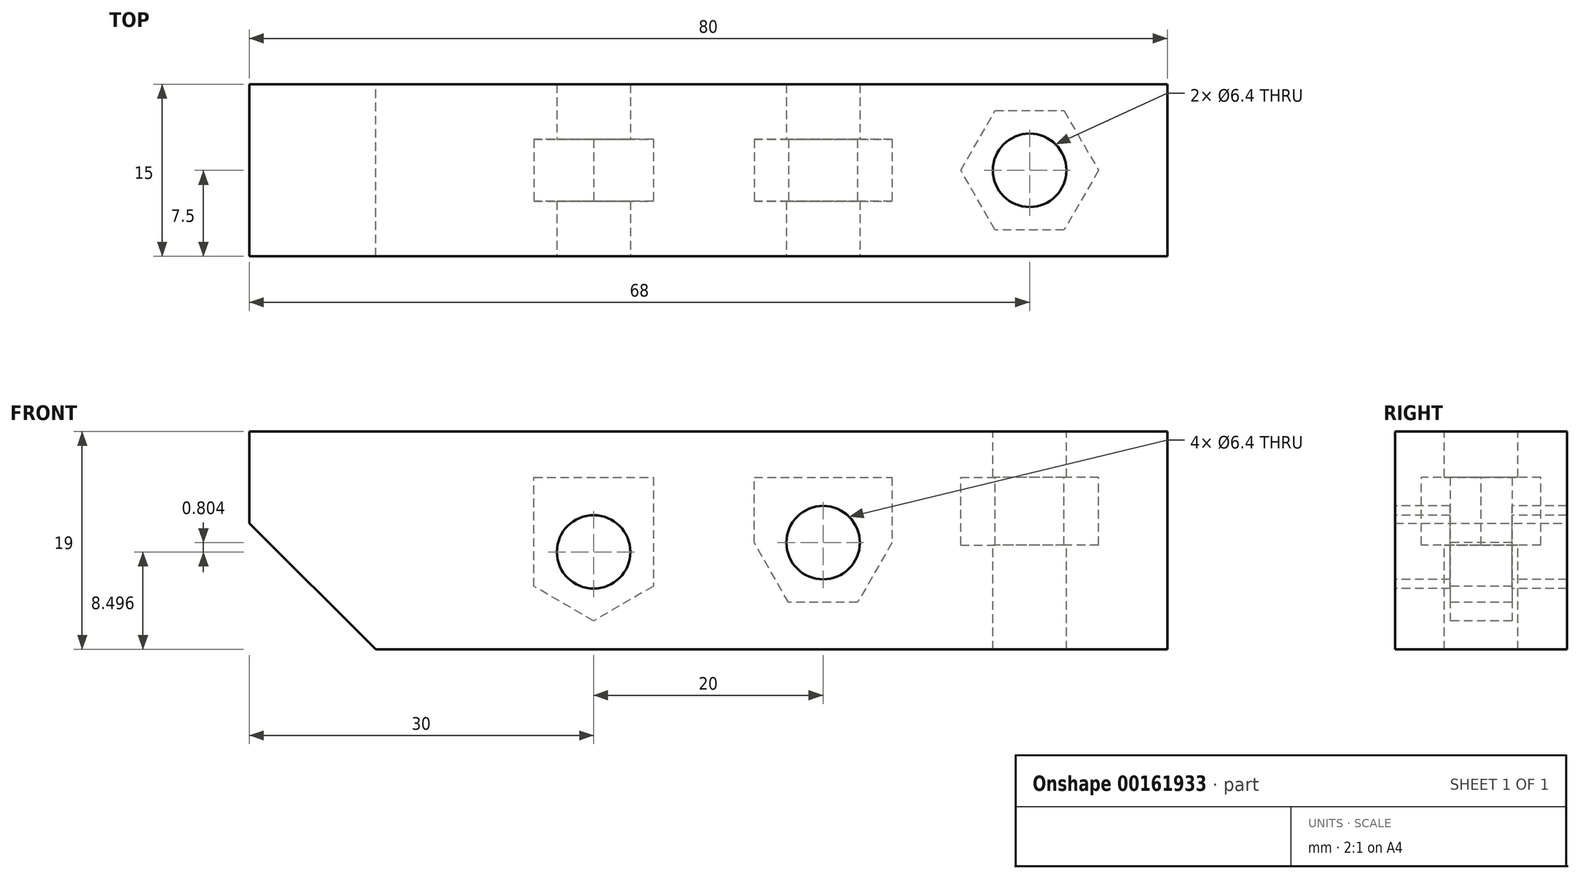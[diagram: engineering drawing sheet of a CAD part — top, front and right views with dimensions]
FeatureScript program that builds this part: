
annotation { "Feature Type Name" : "Feature", "Feature Type Description" : "" }
export const myFeature = defineFeature(function(context is Context, id is Id, definition is map)
    precondition{}
    {
        {
            var Q0;
            Q0=qCreatedBy(makeId("Front.planeOp"),FACE);
            var sketch = newSketch(context, id + "F0", { "sketchPlane" : qUnion([Q0])});
            skLineSegment(sketch, "E0", {"start": v(0, 0) * mm, "end": v(-69, 0) * mm});
            skLineSegment(sketch, "E1", {"start": v(-69, 0) * mm, "end": v(-80, 11) * mm});
            skLineSegment(sketch, "E2", {"start": v(-80, 11) * mm, "end": v(-80, 15) * mm});
            skLineSegment(sketch, "E3", {"start": v(-80, 15) * mm, "end": v(0, 15) * mm});
            skLineSegment(sketch, "E4", {"start": v(0, 15) * mm, "end": v(0, 0) * mm});
            skSolve(sketch);
        }
        {
            var Q0;
            Q0=makeQuery(id+"F0.imprint","IMPRINT",FACE,{"disambiguationData":[TD([[makeQuery(id+"F0.imprint","IMPRINT",EDGE,{"derivedFrom":sQuery(id+"F0.wireOp",EDGE,"E0")}),-1.0]])]});
            extrude(context, id + "F1", {"entities" : qUnion([Q0]), "endBound" : BoundingType.SYMMETRIC, "depth" : 15 * mm});
        }
        {
            var Q0;
            Q0=makeQuery(id+"F1.opExtrude","SWEPT_FACE",FACE,{"disambiguationData":[OSD([sQuery(id+"F0.wireOp",EDGE,"E3")])]});
            var sketch = newSketch(context, id + "F2", { "sketchPlane" : qUnion([Q0])});
            skLineSegment(sketch, "E5", {"start": v(0, 0) * mm, "end": v(-80, 0) * mm, "construction": true});
            skCircle(sketch, "E6", {"center": v(-12, 0) * mm, "radius": 3.2 * mm});
            skSolve(sketch);
        }
        {
            var Q0;
            Q0=makeQuery(id+"F2.imprint","IMPRINT",FACE,{"disambiguationData":[TD([[makeQuery(id+"F2.imprint","IMPRINT",EDGE,{"derivedFrom":sQuery(id+"F2.wireOp",EDGE,"E6")}),1.0]])]});
            extrude(context, id + "F3", {"entities" : qUnion([Q0]), "operationType" : NewBodyOperationType.REMOVE, "endBound" : BoundingType.THROUGH_ALL, "oppositeDirection" : true, "depth" : 25 * mm});
        }
        {
            var Q0;
            Q0=qCreatedBy(makeId("Front.planeOp"),FACE);
            var sketch = newSketch(context, id + "F4", { "sketchPlane" : qUnion([Q0])});
            skCircle(sketch, "E7.cCircle", {"center": v(-30, 9.3) * mm, "radius": 5.2 * mm, "construction": true});
            skLineSegment(sketch, "E7.0", {"start": v(-27, 14.5) * mm, "end": v(-24, 9.3) * mm, "construction": true});
            skLineSegment(sketch, "E7.1", {"start": v(-24, 9.3) * mm, "end": v(-27, 4.1) * mm});
            skLineSegment(sketch, "E7.2", {"start": v(-27, 4.1) * mm, "end": v(-33, 4.1) * mm});
            skLineSegment(sketch, "E7.3", {"start": v(-33, 4.1) * mm, "end": v(-36, 9.3) * mm});
            skLineSegment(sketch, "E7.4", {"start": v(-36, 9.3) * mm, "end": v(-33, 14.5) * mm, "construction": true});
            skLineSegment(sketch, "E7.5", {"start": v(-33, 14.5) * mm, "end": v(-27, 14.5) * mm, "construction": true});
            skPoint(sketch, "E7.0.midPoint", {"position": v(-25.5, 11.9) * mm});
            skLineSegment(sketch, "E8", {"start": v(-36, 9.3) * mm, "end": v(-36, 15) * mm});
            skLineSegment(sketch, "E9", {"start": v(-36, 15) * mm, "end": v(-24, 15) * mm});
            skLineSegment(sketch, "E10", {"start": v(-24, 15) * mm, "end": v(-24, 9.3) * mm});
            skSolve(sketch);
        }
        {
            var Q0;
            Q0 = qSketchRegion(id + "F4", true);
            extrude(context, id + "F5", {"entities" : qUnion([Q0]), "operationType" : NewBodyOperationType.REMOVE, "endBound" : BoundingType.SYMMETRIC, "oppositeDirection" : true, "depth" : 5.4 * mm});
        }
        {
            var Q0;
            Q0=makeQuery(id+"F1.opExtrude","SWEPT_FACE",FACE,{"disambiguationData":[OSD([sQuery(id+"F0.wireOp",EDGE,"E3")])]});
            var sketch = newSketch(context, id + "F6", { "sketchPlane" : qUnion([Q0])});
            skCircle(sketch, "E11.cCircle", {"center": v(-12, 0) * mm, "radius": 5.2 * mm, "construction": true});
            skLineSegment(sketch, "E11.0", {"start": v(-9, -5.2) * mm, "end": v(-15, -5.2) * mm});
            skLineSegment(sketch, "E11.1", {"start": v(-15, -5.2) * mm, "end": v(-18, 0) * mm});
            skLineSegment(sketch, "E11.2", {"start": v(-18, 0) * mm, "end": v(-15, 5.2) * mm});
            skLineSegment(sketch, "E11.3", {"start": v(-15, 5.2) * mm, "end": v(-9, 5.2) * mm});
            skLineSegment(sketch, "E11.4", {"start": v(-9, 5.2) * mm, "end": v(-6, 0) * mm});
            skLineSegment(sketch, "E11.5", {"start": v(-6, 0) * mm, "end": v(-9, -5.2) * mm});
            skPoint(sketch, "E11.0.midPoint", {"position": v(-12, -5.2) * mm});
            skSolve(sketch);
        }
        {
            var Q0;
            Q0 = qSketchRegion(id + "F6", true);
            extrude(context, id + "F7", {"entities" : qUnion([Q0]), "operationType" : NewBodyOperationType.REMOVE, "oppositeDirection" : true, "depth" : 5.9 * mm});
        }
        {
            var Q0;
            Q0=makeQuery(id+"F1.opExtrude","CAP_FACE",FACE,{"disambiguationData":[OSD([sQuery(id+"F0.wireOp",EDGE,"E0"),sQuery(id+"F0.wireOp",EDGE,"E1"),sQuery(id+"F0.wireOp",EDGE,"E2"),sQuery(id+"F0.wireOp",EDGE,"E3"),sQuery(id+"F0.wireOp",EDGE,"E4")])],"isStart":false});
            var sketch = newSketch(context, id + "F8", { "sketchPlane" : qUnion([Q0])});
            skLineSegment(sketch, "E12", {"start": v(-36, 9.3) * mm, "end": v(-24, 9.3) * mm, "construction": true});
            skCircle(sketch, "E13", {"center": v(-30, 9.3) * mm, "radius": 3.2 * mm});
            skSolve(sketch);
        }
        {
            var Q0;
            Q0=makeQuery(id+"F8.imprint","IMPRINT",FACE,{"disambiguationData":[TD([[makeQuery(id+"F8.imprint","IMPRINT",EDGE,{"derivedFrom":sQuery(id+"F8.wireOp",EDGE,"E13")}),1.0]])]});
            var Q1;
            Q1=sQuery(id+"F8.wireOp",EDGE,"E13");
            extrude(context, id + "F9", {"entities" : qUnion([Q0]), "operationType" : NewBodyOperationType.REMOVE, "surfaceEntities" : qUnion([Q1]), "endBound" : BoundingType.THROUGH_ALL, "oppositeDirection" : true, "depth" : 25 * mm});
        }
        {
            var Q0;
            Q0=qCreatedBy(makeId("Front.planeOp"),FACE);
            var sketch = newSketch(context, id + "F10", { "sketchPlane" : qUnion([Q0])});
            skCircle(sketch, "E14.cCircle", {"center": v(-50, 8.5) * mm, "radius": 5.2 * mm, "construction": true});
            skLineSegment(sketch, "E14.0", {"start": v(-44.8, 5.5) * mm, "end": v(-50, 2.5) * mm});
            skLineSegment(sketch, "E14.1", {"start": v(-50, 2.5) * mm, "end": v(-55.2, 5.5) * mm});
            skLineSegment(sketch, "E14.2", {"start": v(-55.2, 5.5) * mm, "end": v(-55.2, 11.5) * mm});
            skLineSegment(sketch, "E14.3", {"start": v(-55.2, 11.5) * mm, "end": v(-50, 14.5) * mm, "construction": true});
            skLineSegment(sketch, "E14.4", {"start": v(-50, 14.5) * mm, "end": v(-44.8, 11.5) * mm, "construction": true});
            skLineSegment(sketch, "E14.5", {"start": v(-44.8, 11.5) * mm, "end": v(-44.8, 5.5) * mm});
            skPoint(sketch, "E14.0.midPoint", {"position": v(-47.4, 4) * mm});
            skLineSegment(sketch, "E15", {"start": v(-55.2, 11.5) * mm, "end": v(-55.2, 15) * mm});
            skLineSegment(sketch, "E16", {"start": v(-55.2, 15) * mm, "end": v(-44.8, 15) * mm});
            skLineSegment(sketch, "E17", {"start": v(-44.8, 15) * mm, "end": v(-44.8, 11.5) * mm});
            skSolve(sketch);
        }
        {
            var Q0;
            Q0 = qSketchRegion(id + "F10", true);
            extrude(context, id + "F11", {"entities" : qUnion([Q0]), "operationType" : NewBodyOperationType.REMOVE, "endBound" : BoundingType.SYMMETRIC, "oppositeDirection" : true, "depth" : 5.4 * mm});
        }
        {
            var Q0;
            Q0=makeQuery(id+"F1.opExtrude","CAP_FACE",FACE,{"disambiguationData":[OSD([sQuery(id+"F0.wireOp",EDGE,"E0"),sQuery(id+"F0.wireOp",EDGE,"E1"),sQuery(id+"F0.wireOp",EDGE,"E2"),sQuery(id+"F0.wireOp",EDGE,"E3"),sQuery(id+"F0.wireOp",EDGE,"E4")])],"isStart":false});
            var sketch = newSketch(context, id + "F12", { "sketchPlane" : qUnion([Q0])});
            skCircle(sketch, "E18", {"center": v(-50, 8.5) * mm, "radius": 3.2 * mm});
            skSolve(sketch);
        }
        {
            var Q0;
            Q0=makeQuery(id+"F12.imprint","IMPRINT",FACE,{"disambiguationData":[TD([[makeQuery(id+"F12.imprint","IMPRINT",EDGE,{"derivedFrom":sQuery(id+"F12.wireOp",EDGE,"E18")}),1.0]])]});
            extrude(context, id + "F13", {"entities" : qUnion([Q0]), "operationType" : NewBodyOperationType.REMOVE, "endBound" : BoundingType.THROUGH_ALL, "oppositeDirection" : true, "depth" : 25 * mm});
        }
        {
            var Q0;
            Q0=makeQuery(id+"F1.opExtrude","SWEPT_FACE",FACE,{"disambiguationData":[OSD([sQuery(id+"F0.wireOp",EDGE,"E1")])]});
            cPlane(context, id + "F14", {"entities" : qUnion([Q0]), "cplaneType" : CPlaneType.OFFSET, "offset" : 4 * mm, "oppositeDirection" : true, "width" : 150 * mm, "height" : 150 * mm});
        }
        {
            var Q0;
            Q0=qCreatedBy(id+"F14.planeOp",FACE);
            var sketch = newSketch(context, id + "F15", { "sketchPlane" : qUnion([Q0])});
            skCircle(sketch, "E19.cCircle", {"center": v(-54.35, 0) * mm, "radius": 5.2 * mm, "construction": true});
            skLineSegment(sketch, "E19.0", {"start": v(-51.34, 5.2) * mm, "end": v(-48.34, 0) * mm});
            skLineSegment(sketch, "E19.1", {"start": v(-48.34, 0) * mm, "end": v(-51.34, -5.2) * mm});
            skLineSegment(sketch, "E19.2", {"start": v(-51.34, -5.2) * mm, "end": v(-57.35, -5.2) * mm});
            skLineSegment(sketch, "E19.3", {"start": v(-57.35, -5.2) * mm, "end": v(-60.35, 0) * mm, "construction": true});
            skLineSegment(sketch, "E19.4", {"start": v(-60.35, 0) * mm, "end": v(-57.35, 5.2) * mm, "construction": true});
            skLineSegment(sketch, "E19.5", {"start": v(-57.35, 5.2) * mm, "end": v(-51.34, 5.2) * mm});
            skPoint(sketch, "E19.0.midPoint", {"position": v(-49.84, 2.6) * mm});
            skLineSegment(sketch, "E20", {"start": v(-57.35, -5.2) * mm, "end": v(-66, -5.2) * mm});
            skLineSegment(sketch, "E21", {"start": v(-66, -5.2) * mm, "end": v(-66, 5.2) * mm});
            skLineSegment(sketch, "E22", {"start": v(-66, 5.2) * mm, "end": v(-57.35, 5.2) * mm});
            skSolve(sketch);
        }
        {
            var Q0;
            Q0 = qSketchRegion(id + "F15", true);
            extrude(context, id + "F16", {"entities" : qUnion([Q0]), "operationType" : NewBodyOperationType.REMOVE, "oppositeDirection" : true, "depth" : 5.4 * mm});
        }
        {
            var Q0;
            Q0=makeQuery(id+"F1.opExtrude","SWEPT_FACE",FACE,{"disambiguationData":[OSD([sQuery(id+"F0.wireOp",EDGE,"E3")])]});
            var sketch = newSketch(context, id + "F17", { "sketchPlane" : qUnion([Q0])});
            skLineSegment(sketch, "E23.bottom", {"start": v(-80, 7.5) * mm, "end": v(0, 7.5) * mm});
            skLineSegment(sketch, "E23.top", {"start": v(-80, -7.5) * mm, "end": v(0, -7.5) * mm});
            skLineSegment(sketch, "E23.left", {"start": v(-80, 7.5) * mm, "end": v(-80, -7.5) * mm});
            skLineSegment(sketch, "E23.right", {"start": v(0, 7.5) * mm, "end": v(0, -7.5) * mm});
            skSolve(sketch);
        }
        {
            var Q0;
            Q0 = qSketchRegion(id + "F17", true);
            extrude(context, id + "F18", {"entities" : qUnion([Q0]), "operationType" : NewBodyOperationType.ADD, "depth" : 4 * mm});
        }
        {
            var Q0;
            Q0=makeQuery(id+"F1.opExtrude","SWEPT_FACE",FACE,{"disambiguationData":[OSD([sQuery(id+"F0.wireOp",EDGE,"E1")])]});
            var sketch = newSketch(context, id + "F19", { "sketchPlane" : qUnion([Q0])});
            skCircle(sketch, "E24", {"center": v(-54.35, 0) * mm, "radius": 3.2 * mm});
            skSolve(sketch);
        }
        {
            var Q0;
            Q0 = qSketchRegion(id + "F19", true);
            extrude(context, id + "F20", {"entities" : qUnion([Q0]), "operationType" : NewBodyOperationType.REMOVE, "oppositeDirection" : true, "depth" : 13 * mm});
        }
        {
            var Q0;
            Q0=makeQuery(id+"F18.opExtrude","CAP_FACE",FACE,{"disambiguationData":[OSD([sQuery(id+"F17.wireOp",EDGE,"E23.bottom"),sQuery(id+"F17.wireOp",EDGE,"E23.top"),sQuery(id+"F17.wireOp",EDGE,"E23.left"),sQuery(id+"F17.wireOp",EDGE,"E23.right")])],"isStart":false});
            var sketch = newSketch(context, id + "F21", { "sketchPlane" : qUnion([Q0])});
            skCircle(sketch, "E25", {"center": v(-12, 0) * mm, "radius": 3.2 * mm});
            skSolve(sketch);
        }
        {
            var Q0;
            Q0 = qSketchRegion(id + "F21", true);
            extrude(context, id + "F22", {"entities" : qUnion([Q0]), "operationType" : NewBodyOperationType.REMOVE, "endBound" : BoundingType.UP_TO_NEXT, "oppositeDirection" : true, "depth" : 25 * mm});
        }
    });
